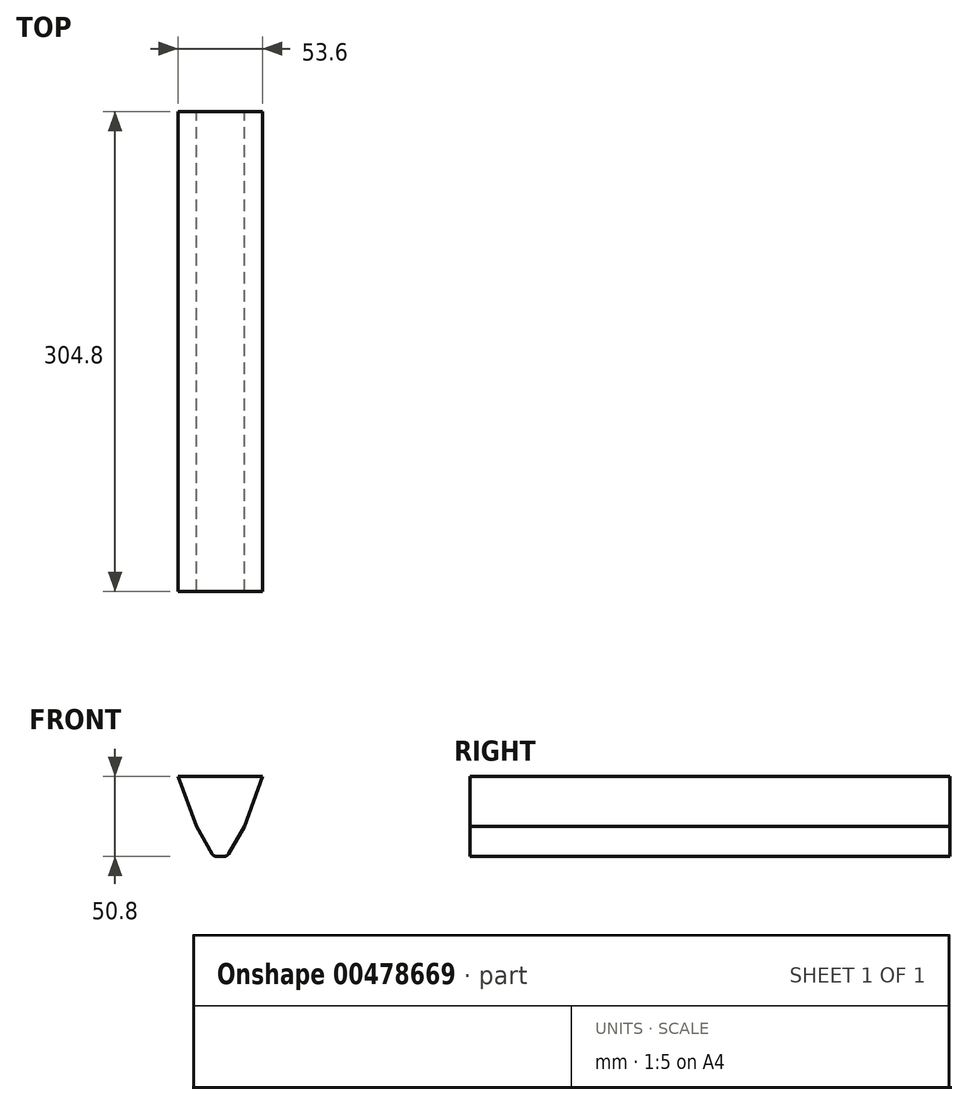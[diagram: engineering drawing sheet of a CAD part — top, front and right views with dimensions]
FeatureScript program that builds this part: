
annotation { "Feature Type Name" : "Feature", "Feature Type Description" : "" }
export const myFeature = defineFeature(function(context is Context, id is Id, definition is map)
    precondition{}
    {
        {
            var Q0;
            Q0=qCreatedBy(makeId("Front.planeOp"),FACE);
            var sketch = newSketch(context, id + "F0", { "sketchPlane" : qUnion([Q0])});
            skLineSegment(sketch, "E0", {"start": v(0, 0) * mm, "end": v(0, 50.8) * mm});
            skLineSegment(sketch, "E1", {"start": v(0, 50.8) * mm, "end": v(26.8, 50.8) * mm});
            skLineSegment(sketch, "E2", {"start": v(26.8, 50.8) * mm, "end": v(15.24, 19.05) * mm});
            skLineSegment(sketch, "E3", {"start": v(15.24, 19.05) * mm, "end": v(5.16, 1.59) * mm});
            skLineSegment(sketch, "E4", {"start": v(2.4, 0) * mm, "end": v(0, 0) * mm});
            skPoint(sketch, "E5.visualSharp", {"position": v(4.24, 0) * mm});
            skArc(sketch, "E5.filletArc", {"start": v(2.4, 0) * mm, "mid": v(4, 0.43) * mm, "end": v(5.16, 1.59) * mm});
            skSolve(sketch);
        }
        {
            var Q0;
            Q0=makeQuery(id+"F0.imprint","IMPRINT",FACE,{"disambiguationData":[TD([[makeQuery(id+"F0.imprint","IMPRINT",EDGE,{"derivedFrom":sQuery(id+"F0.wireOp",EDGE,"E0")}),-1.0]])]});
            extrude(context, id + "F1", {"entities" : qUnion([Q0]), "depth" : 304.8 * mm});
        }
        {
            var Q0;
            Q0=makeQuery(id+"F1.opExtrude","SWEPT_BODY",BODY,{"disambiguationData":[OSD([sQuery(id+"F0.wireOp",EDGE,"E0"),sQuery(id+"F0.wireOp",EDGE,"E1"),sQuery(id+"F0.wireOp",EDGE,"E2"),sQuery(id+"F0.wireOp",EDGE,"E3"),sQuery(id+"F0.wireOp",EDGE,"E4"),sQuery(id+"F0.wireOp",EDGE,"E5.filletArc")])]});
            var Q1;
            Q1=makeQuery(id+"F1.opExtrude","SWEPT_FACE",FACE,{"disambiguationData":[OSD([sQuery(id+"F0.wireOp",EDGE,"E0")])]});
            mirror(context, id + "F2", {"operationType" : NewBodyOperationType.ADD, "entities" : qUnion([Q0]), "mirrorPlane" : qUnion([Q1])});
        }
    });
